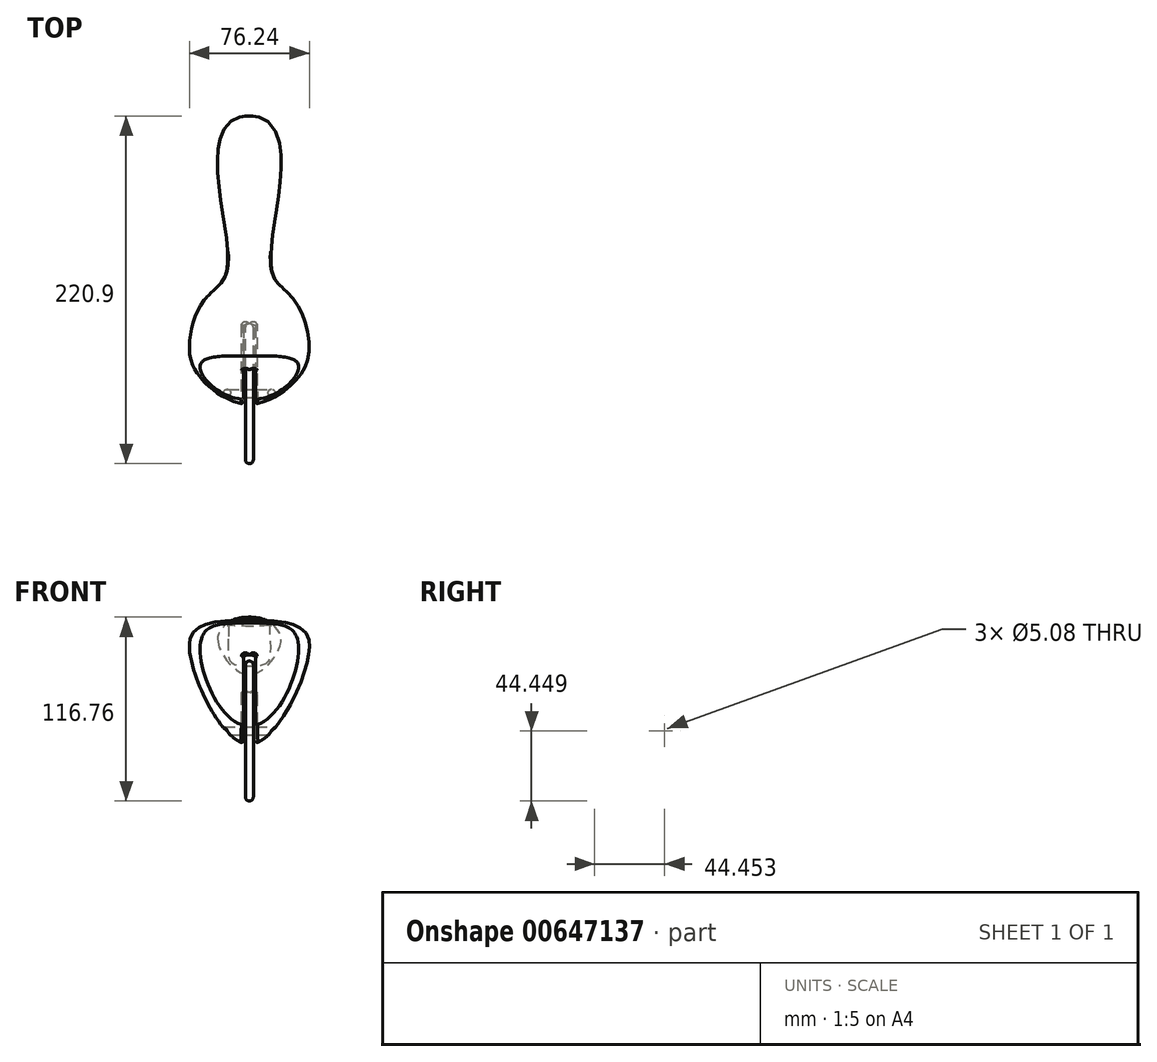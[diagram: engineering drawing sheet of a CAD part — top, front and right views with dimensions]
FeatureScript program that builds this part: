
annotation { "Feature Type Name" : "Feature", "Feature Type Description" : "" }
export const myFeature = defineFeature(function(context is Context, id is Id, definition is map)
    precondition{}
    {
        {
            var Q0;
            Q0=qCreatedBy(makeId("Top.planeOp"),FACE);
            cPlane(context, id + "F0", {"entities" : qUnion([Q0]), "cplaneType" : CPlaneType.OFFSET, "offset" : 12.7 * mm, "width" : 152.4 * mm, "height" : 152.4 * mm});
        }
        {
            var Q0;
            Q0=qCreatedBy(makeId("Right.planeOp"),FACE);
            var sketch = newSketch(context, id + "F1", { "sketchPlane" : qUnion([Q0])});
            skFitSpline(sketch, "E0", {"points": [v(0, 22.63) * mm, v(31.69, 21) * mm, v(103.66, 26.37) * mm, v(152.4, 12.7) * mm], "startDerivative": vector(24.11, 56.35) * mm, "endDerivative": vector(0, -91.8) * mm});
            skFitSpline(sketch, "E1", {"points": [v(152.4, 12.7) * mm, v(123.34, -10.02) * mm, v(34.56, -13.34) * mm, v(-27.97, -42.75) * mm], "startDerivative": vector(0, -121.83) * mm, "endDerivative": vector(121.15, 283.17) * mm});
            skCircle(sketch, "E2", {"center": v(-24.05, -45.9) * mm, "radius": 50.8 * mm, "construction": true});
            skLineSegment(sketch, "E3", {"start": v(0, 22.63) * mm, "end": v(-27.97, -42.75) * mm});
            skSolve(sketch);
        }
        {
            var Q0;
            Q0=qCreatedBy(id+"F0.planeOp",FACE);
            var sketch = newSketch(context, id + "F2", { "sketchPlane" : qUnion([Q0])});
            skLineSegment(sketch, "E4", {"start": v(30.48, -4.25) * mm, "end": v(0, -4.25) * mm});
            skLineSegment(sketch, "E5", {"start": v(0, -4.25) * mm, "end": v(0, 152.4) * mm, "construction": true});
            skFitSpline(sketch, "E6", {"points": [v(30.48, -4.25) * mm, v(31.84, 30.36) * mm, v(14.9, 51.38) * mm, v(19.5, 109.76) * mm, v(0, 152.4) * mm], "startDerivative": vector(142.97, 0) * mm, "endDerivative": vector(-227.78, 0) * mm});
            skLineSegment(sketch, "E7.MirrorCS", {"start": v(-30.48, -4.25) * mm, "end": v(0, -4.25) * mm});
            skFitSpline(sketch, "E8.MirrorCS", {"points": [v(-30.48, -4.25) * mm, v(-31.84, 30.36) * mm, v(-14.9, 51.38) * mm, v(-19.5, 109.76) * mm, v(0, 152.4) * mm], "startDerivative": vector(-142.97, 0) * mm, "endDerivative": vector(227.78, 0) * mm});
            skSolve(sketch);
        }
        {
            var Q0;
            Q0=sQuery(id+"F1.wireOp",VERTEX,"E0.start");
            var Q1;
            Q1=sQuery(id+"F2.wireOp",VERTEX,"E5.start");
            var Q2;
            Q2=sQuery(id+"F2.wireOp",VERTEX,"E6.start");
            cPlane(context, id + "F3", {"entities" : qUnion([Q0, Q1, Q2]), "cplaneType" : CPlaneType.THREE_POINT, "offset" : 152.4 * mm, "width" : 152.4 * mm, "height" : 152.4 * mm});
        }
        {
            var Q0;
            Q0=qCreatedBy(id+"F3.planeOp",FACE);
            var sketch = newSketch(context, id + "F4", { "sketchPlane" : qUnion([Q0])});
            skLineSegment(sketch, "E9", {"start": v(0, 33.33) * mm, "end": v(0, -50.3) * mm, "construction": true});
            skFitSpline(sketch, "E10", {"points": [v(0, 20.8) * mm, v(30.48, 10) * mm, v(0, -50.3) * mm], "startDerivative": vector(106.7, 0) * mm, "endDerivative": vector(-99.08, 0) * mm});
            skFitSpline(sketch, "E11.MirrorCS", {"points": [v(0, 20.8) * mm, v(-30.48, 10) * mm, v(0, -50.3) * mm], "startDerivative": vector(-106.7, 0) * mm, "endDerivative": vector(99.08, 0) * mm});
            skSolve(sketch);
        }
        {
            var Q0;
            Q0=sQuery(id+"F2.wireOp",VERTEX,"E6.3.internal");
            var Q1;
            Q1=qCreatedBy(makeId("Front.planeOp"),FACE);
            cPlane(context, id + "F5", {"entities" : qUnion([Q0, Q1]), "cplaneType" : CPlaneType.PLANE_POINT, "offset" : 152.4 * mm, "width" : 152.4 * mm, "height" : 152.4 * mm});
        }
        {
            var Q0;
            Q0=qCreatedBy(id+"F5.planeOp",FACE);
            var sketch = newSketch(context, id + "F6", { "sketchPlane" : qUnion([Q0])});
            skFitSpline(sketch, "E12", {"points": [v(0, 26.4) * mm, v(19.5, 12.7) * mm, v(0, -9.75) * mm], "startDerivative": vector(68.63, 0) * mm, "endDerivative": vector(-57.85, 0) * mm});
            skLineSegment(sketch, "E13", {"start": v(0, 26.4) * mm, "end": v(0, 7.7) * mm, "construction": true});
            skFitSpline(sketch, "E14.MirrorCS", {"points": [v(0, 26.4) * mm, v(-19.5, 12.7) * mm, v(0, -9.75) * mm], "startDerivative": vector(-68.63, 0) * mm, "endDerivative": vector(57.85, 0) * mm});
            skSolve(sketch);
        }
        {
            var Q0;
            Q0=makeQuery(id+"F4.imprint","IMPRINT",FACE,{"disambiguationData":[TD([[makeQuery(id+"F4.imprint","IMPRINT",EDGE,{"derivedFrom":sQuery(id+"F4.wireOp",EDGE,"E10")}),-1.0]])]});
            var Q1;
            Q1=makeQuery(id+"F6.imprint","IMPRINT",FACE,{"disambiguationData":[TD([[makeQuery(id+"F6.imprint","IMPRINT",EDGE,{"derivedFrom":sQuery(id+"F6.wireOp",EDGE,"E12")}),-1.0]])]});
            var Q2;
            Q2=sQuery(id+"F2.wireOp",VERTEX,"E6.end");
            var Q3;
            Q3=sQuery(id+"F2.wireOp",EDGE,"E6");
            var Q4;
            Q4=sQuery(id+"F2.wireOp",EDGE,"E8.MirrorCS");
            var Q5;
            Q5=sQuery(id+"F1.wireOp",EDGE,"E1");
            var Q6;
            Q6=sQuery(id+"F1.wireOp",EDGE,"E0");
            loft(context, id + "F7", {"addGuides" : true, "sheetProfilesArray" : [{ "sheetProfileEntities" : qUnion([Q0]) }, { "sheetProfileEntities" : qUnion([Q1]) }, { "sheetProfileEntities" : qUnion([Q2]) }], "guidesArray" : [{ "guideEntities" : qUnion([Q3]), "guideDerivativeType" : LoftGuideDerivativeType.DEFAULT, "guideDerivativeMagnitude" : 1 }, { "guideEntities" : qUnion([Q4]), "guideDerivativeType" : LoftGuideDerivativeType.DEFAULT, "guideDerivativeMagnitude" : 1 }, { "guideEntities" : qUnion([Q5]), "guideDerivativeType" : LoftGuideDerivativeType.DEFAULT, "guideDerivativeMagnitude" : 1 }, { "guideEntities" : qUnion([Q6]), "guideDerivativeType" : LoftGuideDerivativeType.DEFAULT, "guideDerivativeMagnitude" : 1 }]});
        }
        {
            var Q0;
            Q0=qCreatedBy(makeId("Right.planeOp"),FACE);
            var sketch = newSketch(context, id + "F8", { "sketchPlane" : qUnion([Q0])});
            skCircle(sketch, "E15.0", {"center": v(-24.05, -45.9) * mm, "radius": 50.8 * mm});
            skSolve(sketch);
        }
        {
            var Q0;
            Q0=makeQuery(id+"F8.imprint","IMPRINT",FACE,{"disambiguationData":[TD([[makeQuery(id+"F8.imprint","IMPRINT",EDGE,{"derivedFrom":sQuery(id+"F8.wireOp",EDGE,"E15.0")}),1.0]])]});
            extrude(context, id + "F9", {"entities" : qUnion([Q0]), "operationType" : NewBodyOperationType.REMOVE, "endBound" : BoundingType.SYMMETRIC, "oppositeDirection" : true, "depth" : 7.62 * mm});
        }
        {
            var Q0;
            Q0=makeQuery(id+"F9.boolean.opBoolean","COPY",FACE,{"derivedFrom":makeQuery(id+"F9.opExtrude","CAP_FACE",FACE,{"disambiguationData":[OSD([sQuery(id+"F8.wireOp",EDGE,"E15.0")])],"isStart":false})});
            var Q1;
            Q1=makeQuery(id+"F9.boolean.opBoolean","COPY",FACE,{"derivedFrom":makeQuery(id+"F9.opExtrude","CAP_FACE",FACE,{"disambiguationData":[OSD([sQuery(id+"F8.wireOp",EDGE,"E15.0")])],"isStart":true})});
            fillet(context, id + "F10", {"entities" : qUnion([Q0, Q1]), "radius" : 1.27 * mm, "tangentPropagation" : true, "allowEdgeOverflow" : false});
        }
        {
            var Q0;
            Q0=qCreatedBy(makeId("Right.planeOp"),FACE);
            var sketch = newSketch(context, id + "F11", { "sketchPlane" : qUnion([Q0])});
            skCircle(sketch, "E16", {"center": v(-24.05, -45.9) * mm, "radius": 44.45 * mm});
            skSolve(sketch);
        }
        {
            var Q0;
            Q0=makeQuery(id+"F11.imprint","IMPRINT",FACE,{"disambiguationData":[TD([[makeQuery(id+"F11.imprint","IMPRINT",EDGE,{"derivedFrom":sQuery(id+"F11.wireOp",EDGE,"E16")}),1.0]])]});
            extrude(context, id + "F12", {"entities" : qUnion([Q0]), "endBound" : BoundingType.SYMMETRIC, "depth" : 5.08 * mm});
        }
        {
            var Q0;
            Q0=makeQuery(id+"F12.opExtrude","SWEPT_FACE",FACE,{"disambiguationData":[OSD([sQuery(id+"F11.wireOp",EDGE,"E16")])]});
            fillet(context, id + "F13", {"entities" : qUnion([Q0]), "radius" : 2.54 * mm, "tangentPropagation" : true, "allowEdgeOverflow" : false});
        }
        {
            var Q0;
            Q0=qCreatedBy(makeId("Right.planeOp"),FACE);
            var sketch = newSketch(context, id + "F14", { "sketchPlane" : qUnion([Q0])});
            skCircle(sketch, "E17", {"center": v(-24.05, -45.9) * mm, "radius": 2.54 * mm});
            skSolve(sketch);
        }
        {
            var Q0;
            Q0=qSketchRegion(id+"F14",true);
            extrude(context, id + "F15", {"entities" : qUnion([Q0]), "operationType" : NewBodyOperationType.REMOVE, "endBound" : BoundingType.THROUGH_ALL, "oppositeDirection" : true, "depth" : 25.4 * mm, "hasSecondDirection" : true, "secondDirectionBound" : SecondDirectionBoundingType.THROUGH_ALL, "secondDirectionOppositeDirection" : false, "secondDirectionDepth" : 25.4 * mm});
        }
    });
